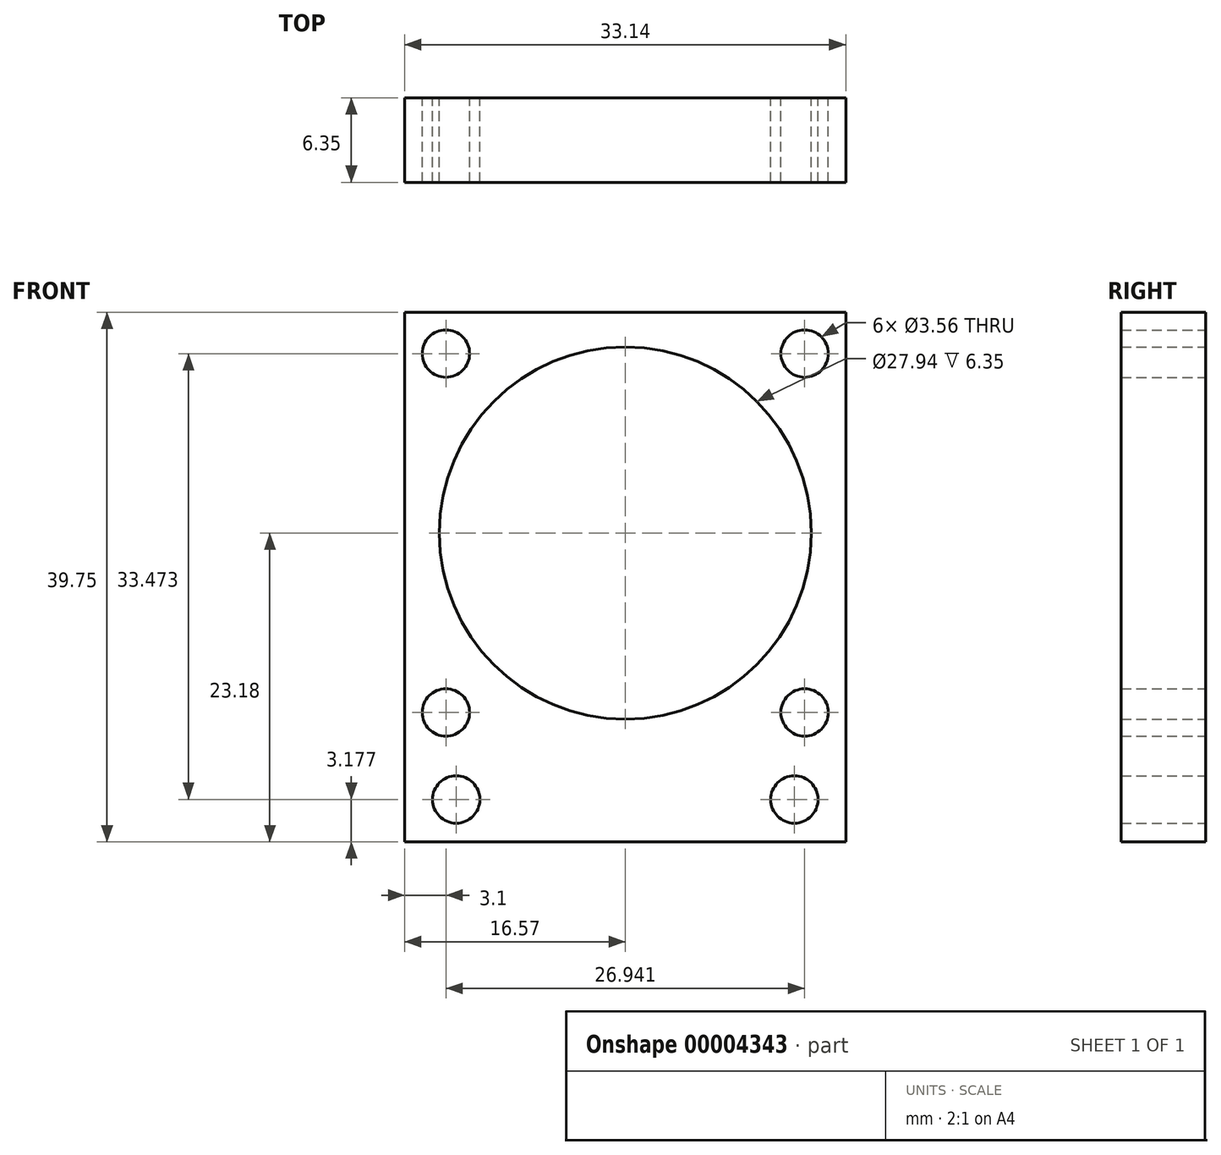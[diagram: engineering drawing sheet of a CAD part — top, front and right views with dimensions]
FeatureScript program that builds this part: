
annotation { "Feature Type Name" : "Feature", "Feature Type Description" : "" }
export const myFeature = defineFeature(function(context is Context, id is Id, definition is map)
    precondition{}
    {
        {
            var Q0;
            Q0=qCreatedBy(makeId("Front.planeOp"),FACE);
            var sketch = newSketch(context, id + "F0", { "sketchPlane" : qUnion([Q0])});
            skLineSegment(sketch, "E0.rect.bottom", {"start": v(13.47, -13.47) * mm, "end": v(-13.47, -13.47) * mm, "construction": true});
            skLineSegment(sketch, "E0.rect.top", {"start": v(13.47, 13.47) * mm, "end": v(-13.47, 13.47) * mm, "construction": true});
            skLineSegment(sketch, "E0.rect.left", {"start": v(13.47, -13.47) * mm, "end": v(13.47, 13.47) * mm, "construction": true});
            skLineSegment(sketch, "E0.rect.right", {"start": v(-13.47, -13.47) * mm, "end": v(-13.47, 13.47) * mm, "construction": true});
            skPoint(sketch, "E0.rect.middle", {"position": v(0, 0) * mm});
            skCircle(sketch, "E1", {"center": v(-13.47, 13.47) * mm, "radius": 1.78 * mm});
            skCircle(sketch, "E2", {"center": v(13.47, 13.47) * mm, "radius": 1.78 * mm});
            skCircle(sketch, "E3", {"center": v(13.47, -13.47) * mm, "radius": 1.78 * mm});
            skCircle(sketch, "E4", {"center": v(-13.47, -13.47) * mm, "radius": 1.78 * mm});
            skLineSegment(sketch, "E5", {"start": v(-13.47, -13.47) * mm, "end": v(13.47, 13.47) * mm, "construction": true});
            skLineSegment(sketch, "E6.bottom", {"start": v(-16.57, 16.57) * mm, "end": v(16.57, 16.57) * mm});
            skLineSegment(sketch, "E6.top", {"start": v(-16.57, -23.18) * mm, "end": v(16.57, -23.18) * mm});
            skLineSegment(sketch, "E6.left", {"start": v(-16.57, 16.57) * mm, "end": v(-16.57, -23.18) * mm});
            skLineSegment(sketch, "E6.right", {"start": v(16.57, 16.57) * mm, "end": v(16.57, -23.18) * mm});
            skLineSegment(sketch, "E7", {"start": v(13.47, 13.47) * mm, "end": v(16.57, 16.57) * mm, "construction": true});
            skLineSegment(sketch, "E8", {"start": v(-13.47, -13.47) * mm, "end": v(-16.57, -16.57) * mm, "construction": true});
            skLineSegment(sketch, "E9", {"start": v(-16.57, -16.57) * mm, "end": v(16.57, -16.57) * mm, "construction": true});
            skLineSegment(sketch, "E10", {"start": v(-16.57, -16.83) * mm, "end": v(16.57, -16.83) * mm, "construction": true});
            skCircle(sketch, "E11", {"center": v(-12.7, -20) * mm, "radius": 1.78 * mm});
            skCircle(sketch, "E12", {"center": v(12.7, -20) * mm, "radius": 1.78 * mm});
            skLineSegment(sketch, "E13", {"start": v(-12.7, -16.83) * mm, "end": v(-12.7, -23.18) * mm, "construction": true});
            skCircle(sketch, "E14", {"center": v(0, 0) * mm, "radius": 12.7 * mm, "construction": true});
            skCircle(sketch, "E15", {"center": v(0, 0) * mm, "radius": 13.97 * mm});
            skLineSegment(sketch, "E16", {"start": v(-12.7, -20) * mm, "end": v(12.7, -20) * mm, "construction": true});
            skLineSegment(sketch, "E17", {"start": v(0, -23.18) * mm, "end": v(0, -20) * mm, "construction": true});
            skSolve(sketch);
        }
        {
            var Q0;
            Q0=makeQuery(id+"F0.imprint","IMPRINT",FACE,{"disambiguationData":[TD([[makeQuery(id+"F0.imprint","IMPRINT",EDGE,{"derivedFrom":sQuery(id+"F0.wireOp",EDGE,"E1")}),-1.0]])]});
            extrude(context, id + "F1", {"entities" : qUnion([Q0]), "depth" : 6.35 * mm});
        }
    });
